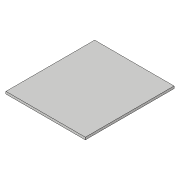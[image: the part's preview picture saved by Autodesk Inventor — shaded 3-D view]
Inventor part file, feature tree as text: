
AUTODESK INVENTOR PART (.ipt)
format: ipt  version: 2018.3 (Build 223284000, 284)  size: 73,216 bytes
history: native  units: in
note: dims shown in document units (in); Inventor stores cm internally (conversion verified against a paired STEP export)
features: extrude x1, sketch x1
ambient origin geometry x8: Origin, YZ Plane, XZ Plane, XY Plane, X Axis, Y Axis, Z Axis, Center Point
bodies: Solid1 (feature_tree)
feature tree (2):
  extrude  "Extrusion1"  Depth=4.75in
  sketch  "Sketch1"  dims[d0=4.25in d1=4.75in d2=0.125in d3=0.0in]
